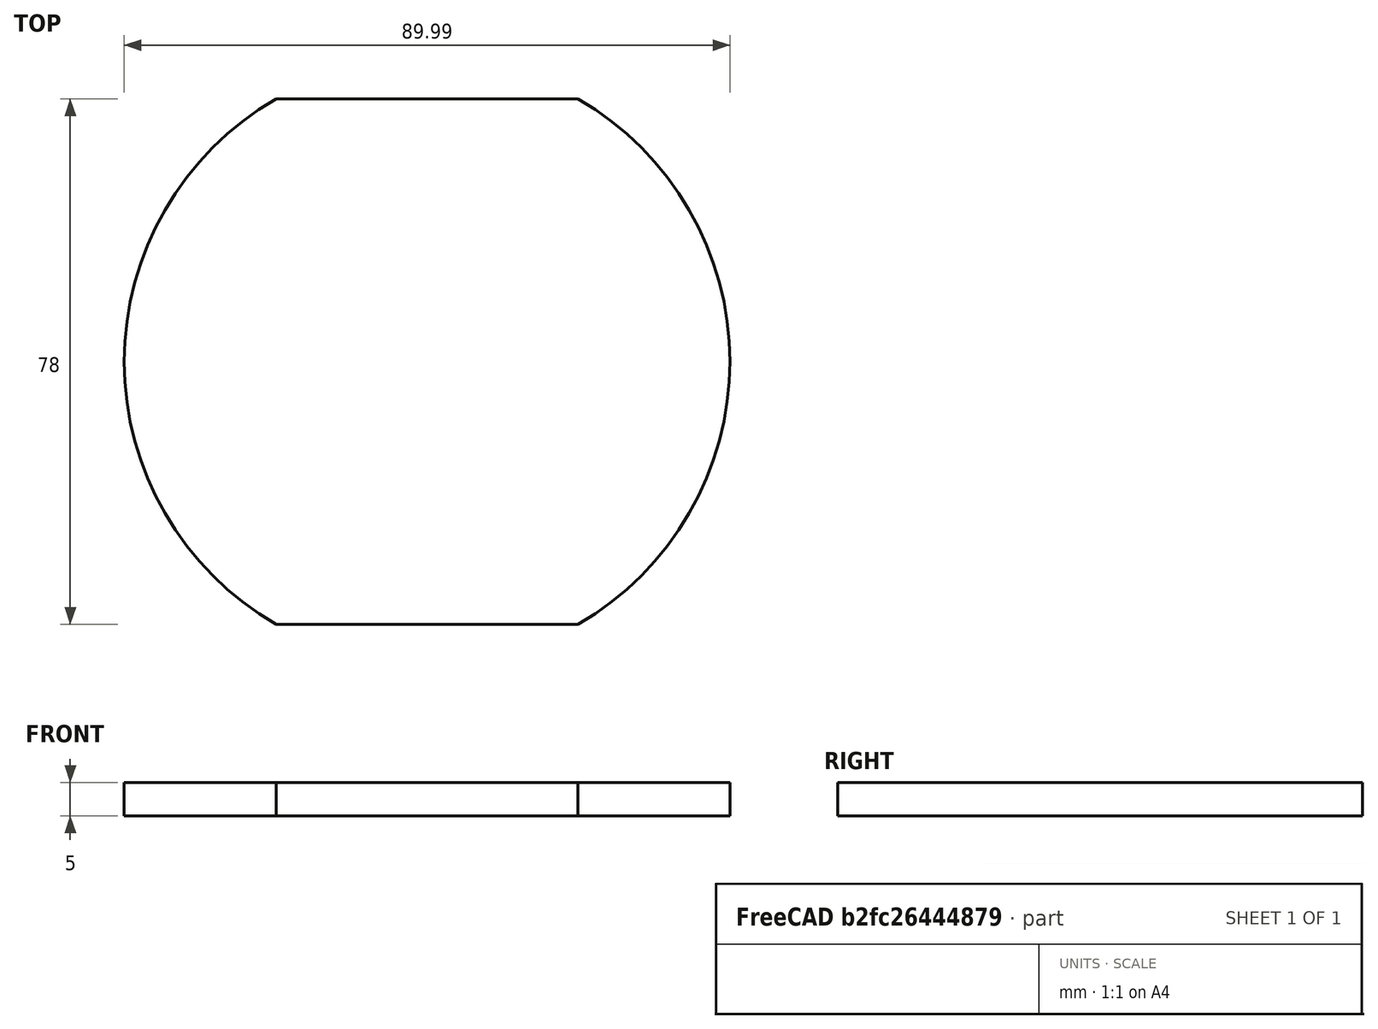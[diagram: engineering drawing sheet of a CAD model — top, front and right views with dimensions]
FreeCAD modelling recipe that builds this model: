
FCSTD DOCUMENT  (FreeCAD 1.0R39319 (Git))
Label: chapa_circle_90mm
License: All rights reserved
LicenseURL: https://en.wikipedia.org/wiki/All_rights_reserved
objects: Sketcher::SketchObject×1, PartDesign::Pad×1, PartDesign::Body×1
note: 6 computed .brp shape members not serialized (recipe doc carries the construction recipe); baked Part::Feature solids carry a one-line shape summary decoded from their .brp

FEATURE [Sketcher::SketchObject] Sketch_1
  ArcFitTolerance = 1e-06
  AttachmentSupport = -> [XY_Plane]
  FullyConstrained = false
  MakeInternals = false
  MapMode = 5
  sketch-geometry (4):
    g0: ArcOfCircle CenterX=0 CenterY=0.0103537 CenterZ=0 NormalX=0 NormalY=0 NormalZ=1 AngleXU=0 Radius=44.991 StartAngle=5.23436 EndAngle=7.33201
    g1: LineSegment StartX=22.4319 StartY=39.0104 StartZ=0 EndX=-22.4499 EndY=39.0104 EndZ=0
    g2: ArcOfCircle CenterX=0 CenterY=0.0155312 CenterZ=0 NormalX=0 NormalY=0 NormalZ=1 AngleXU=0 Radius=44.9955 StartAngle=2.09317 EndAngle=4.19048
    g3: LineSegment StartX=-22.4319 StartY=-38.9896 StartZ=0 EndX=22.4319 EndY=-38.9896 EndZ=0
  constraints (7):
    c: Coincident(g0,g1)
    c: Coincident(g1,g2)
    c: Coincident(g2,g3)
    c: Coincident(g3,g0)
    c: Parallel(g1,g3)
    c: Horizontal(g1)
    c: Distance(g1,g3) = 78
FEATURE [PartDesign::Pad] Pad_1
  Direction = (0,0,1)
  Length = 5
  Length2 = 10
  Profile = -> Sketch_1
  Refine = true
  Suppressed = false
  Type = 0
FEATURE [PartDesign::Body] Body
  AllowCompound = false
  Group = -> [Sketch_1,Pad_1]
  Origin = -> Origin
  Tip = -> Pad_1
